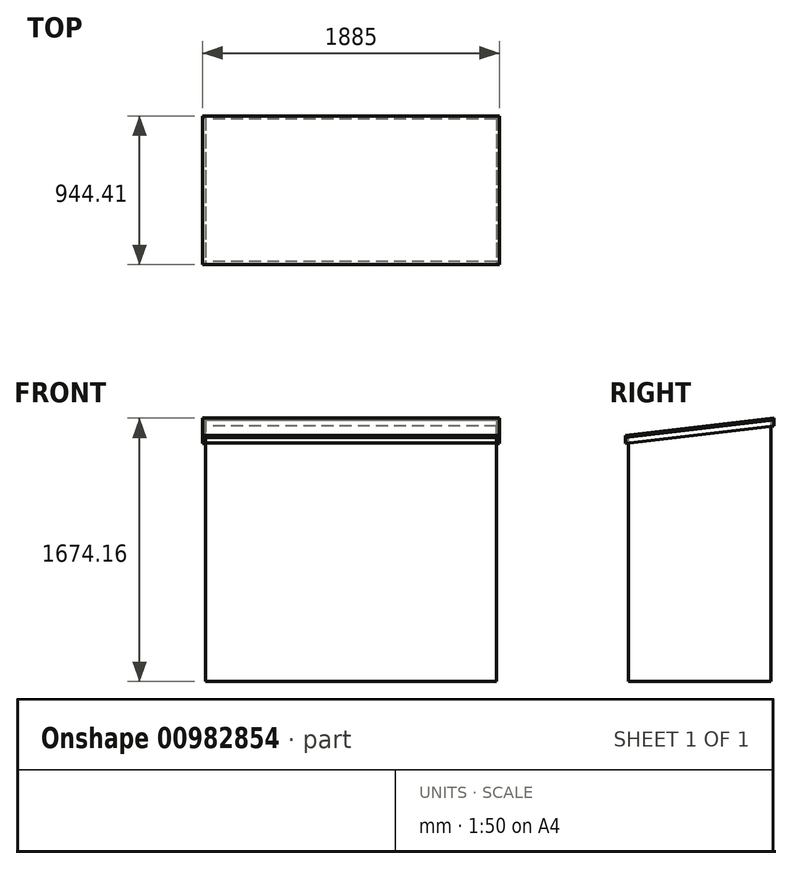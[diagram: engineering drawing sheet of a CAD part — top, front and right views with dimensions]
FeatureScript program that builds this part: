
annotation { "Feature Type Name" : "Feature", "Feature Type Description" : "" }
export const myFeature = defineFeature(function(context is Context, id is Id, definition is map)
    precondition{}
    {
        {
            var Q0;
            Q0=qCreatedBy(makeId("Right.planeOp"),FACE);
            var sketch = newSketch(context, id + "F0", { "sketchPlane" : qUnion([Q0])});
            skLineSegment(sketch, "E0", {"start": v(0, 0) * mm, "end": v(-905, 0) * mm});
            skLineSegment(sketch, "E1", {"start": v(-905, 0) * mm, "end": v(-905, 1553) * mm});
            skLineSegment(sketch, "E2", {"start": v(-905, 1553) * mm, "end": v(0, 1660) * mm});
            skLineSegment(sketch, "E3", {"start": v(0, 1660) * mm, "end": v(0, 0) * mm});
            skSolve(sketch);
        }
        {
            var Q0;
            Q0 = qSketchRegion(id + "F0", true);
            extrude(context, id + "F1", {"entities" : qUnion([Q0]), "depth" : 1847 * mm, "offsetDistance" : 25 * mm});
        }
        {
            var Q0;
            Q0=makeQuery(id+"F1.opExtrude","CAP_FACE",FACE,{"disambiguationData":[OSD([sQuery(id+"F0.wireOp",EDGE,"E0"),sQuery(id+"F0.wireOp",EDGE,"E1"),sQuery(id+"F0.wireOp",EDGE,"E2"),sQuery(id+"F0.wireOp",EDGE,"E3")])],"isStart":true});
            var sketch = newSketch(context, id + "F2", { "sketchPlane" : qUnion([Q0])});
            skLineSegment(sketch, "E4.bottom", {"start": v(905, 1553) * mm, "end": v(924, 1553) * mm});
            skLineSegment(sketch, "E4.top", {"start": v(905, 1515) * mm, "end": v(924, 1515) * mm});
            skLineSegment(sketch, "E4.left", {"start": v(905, 1553) * mm, "end": v(905, 1515) * mm});
            skLineSegment(sketch, "E4.right", {"start": v(924, 1553) * mm, "end": v(924, 1515) * mm});
            skLineSegment(sketch, "E5.bottom", {"start": v(0, 1661.98) * mm, "end": v(-19, 1661.98) * mm});
            skLineSegment(sketch, "E5.top", {"start": v(0, 1623.98) * mm, "end": v(-19, 1623.98) * mm});
            skLineSegment(sketch, "E5.left", {"start": v(0, 1661.98) * mm, "end": v(0, 1623.98) * mm});
            skLineSegment(sketch, "E5.right", {"start": v(-19, 1661.98) * mm, "end": v(-19, 1623.98) * mm});
            skLineSegment(sketch, "E6", {"start": v(-19, 1623.98) * mm, "end": v(-14.54, 1661.72) * mm, "construction": true});
            skSolve(sketch);
        }
        {
            var Q0;
            Q0 = qSketchRegion(id + "F2", true);
            var Q1;
            Q1=makeQuery(id+"F1.opExtrude","CAP_FACE",FACE,{"disambiguationData":[OSD([sQuery(id+"F0.wireOp",EDGE,"E0"),sQuery(id+"F0.wireOp",EDGE,"E1"),sQuery(id+"F0.wireOp",EDGE,"E2"),sQuery(id+"F0.wireOp",EDGE,"E3")])],"isStart":false});
            extrude(context, id + "F3", {"entities" : qUnion([Q0]), "endBound" : BoundingType.UP_TO_SURFACE, "oppositeDirection" : true, "depth" : 25 * mm, "endBoundEntityFace" : qUnion([Q1]), "offsetDistance" : 25 * mm});
        }
        {
            var Q0;
            Q0=makeQuery(id+"F1.opExtrude","CAP_FACE",FACE,{"disambiguationData":[OSD([sQuery(id+"F0.wireOp",EDGE,"E0"),sQuery(id+"F0.wireOp",EDGE,"E1"),sQuery(id+"F0.wireOp",EDGE,"E2"),sQuery(id+"F0.wireOp",EDGE,"E3")])],"isStart":true});
            var sketch = newSketch(context, id + "F4", { "sketchPlane" : qUnion([Q0])});
            skLineSegment(sketch, "E7", {"start": v(-19, 1662.25) * mm, "end": v(924, 1550.75) * mm});
            skLineSegment(sketch, "E8", {"start": v(924, 1550.75) * mm, "end": v(924, 1512.49) * mm});
            skLineSegment(sketch, "E9", {"start": v(924, 1512.49) * mm, "end": v(-19, 1623.98) * mm});
            skLineSegment(sketch, "E10", {"start": v(-19, 1623.98) * mm, "end": v(-19, 1662.25) * mm});
            skLineSegment(sketch, "E11", {"start": v(452.5, 1568.24) * mm, "end": v(456.96, 1605.97) * mm, "construction": true});
            skSolve(sketch);
        }
        {
            var Q0;
            Q0 = qSketchRegion(id + "F4", true);
            extrude(context, id + "F5", {"entities" : qUnion([Q0]), "depth" : 19 * mm, "offsetDistance" : 25 * mm});
        }
        {
            var Q0;
            Q0=makeQuery(id+"F1.opExtrude","CAP_FACE",FACE,{"disambiguationData":[OSD([sQuery(id+"F0.wireOp",EDGE,"E0"),sQuery(id+"F0.wireOp",EDGE,"E1"),sQuery(id+"F0.wireOp",EDGE,"E2"),sQuery(id+"F0.wireOp",EDGE,"E3")])],"isStart":false});
            var sketch = newSketch(context, id + "F6", { "sketchPlane" : qUnion([Q0])});
            skLineSegment(sketch, "E12.0.0", {"start": v(19, 1623.98) * mm, "end": v(-924, 1512.49) * mm});
            skLineSegment(sketch, "E12.0.1", {"start": v(-924, 1512.49) * mm, "end": v(-924, 1550.75) * mm});
            skLineSegment(sketch, "E12.0.2", {"start": v(-924, 1550.75) * mm, "end": v(19, 1662.25) * mm});
            skLineSegment(sketch, "E12.0.3", {"start": v(19, 1662.25) * mm, "end": v(19, 1623.98) * mm});
            skSolve(sketch);
        }
        {
            var Q0;
            Q0 = qSketchRegion(id + "F6", true);
            extrude(context, id + "F7", {"entities" : qUnion([Q0]), "depth" : 19 * mm, "offsetDistance" : 25 * mm});
        }
        {
            var Q0;
            Q0=makeQuery(id+"F1.opExtrude","SWEPT_FACE",FACE,{"disambiguationData":[OSD([sQuery(id+"F0.wireOp",EDGE,"E2")])]});
            var sketch = newSketch(context, id + "F8", { "sketchPlane" : qUnion([Q0])});
            skLineSegment(sketch, "E13.bottom", {"start": v(-19, 214.04) * mm, "end": v(1866, 214.04) * mm});
            skLineSegment(sketch, "E13.top", {"start": v(-19, -735.53) * mm, "end": v(1866, -735.53) * mm});
            skLineSegment(sketch, "E13.left", {"start": v(-19, 214.04) * mm, "end": v(-19, -735.53) * mm});
            skLineSegment(sketch, "E13.right", {"start": v(1866, 214.04) * mm, "end": v(1866, -735.53) * mm});
            skSolve(sketch);
        }
        {
            var Q0;
            Q0 = qSketchRegion(id + "F8", true);
            extrude(context, id + "F9", {"entities" : qUnion([Q0]), "flatOperationType" : FlatOperationType.REMOVE, "depth" : 12 * mm, "offsetDistance" : 25 * mm, "domain" : OperationDomain.MODEL});
        }
    });
